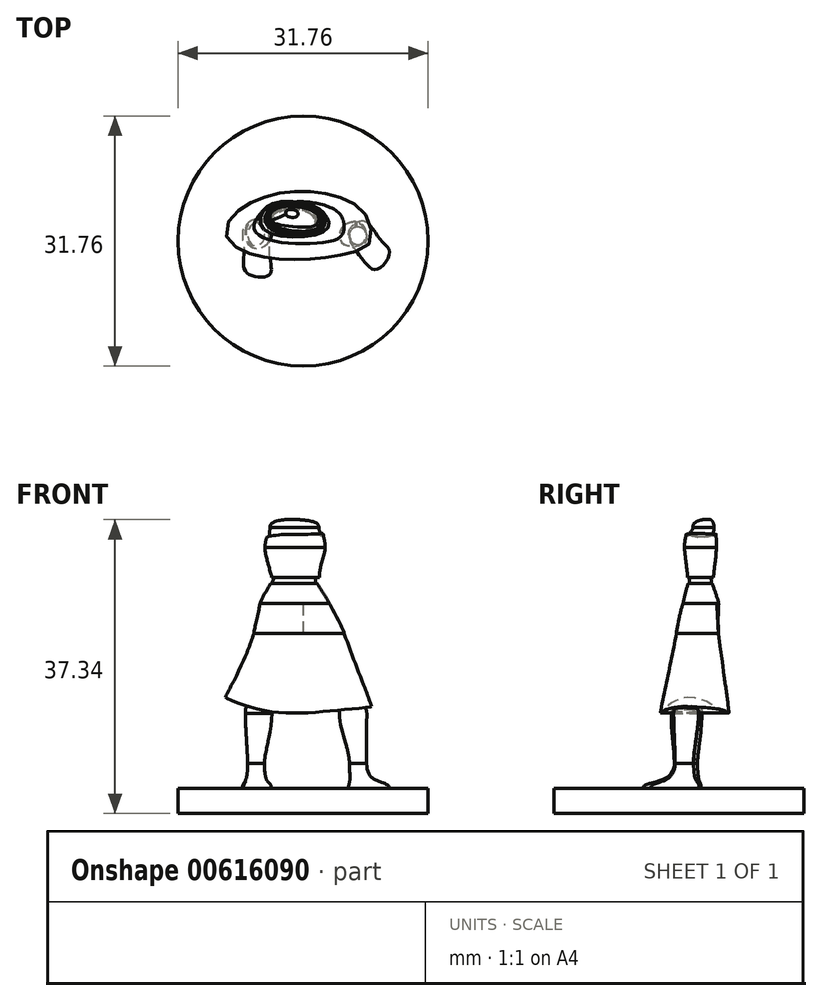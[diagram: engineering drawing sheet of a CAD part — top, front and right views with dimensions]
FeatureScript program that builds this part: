
annotation { "Feature Type Name" : "Feature", "Feature Type Description" : "" }
export const myFeature = defineFeature(function(context is Context, id is Id, definition is map)
    precondition{}
    {
        {
            var Q0;
            Q0=qCreatedBy(makeId("Top.planeOp"),FACE);
            var sketch = newSketch(context, id + "F0", { "sketchPlane" : qUnion([Q0])});
            skCircle(sketch, "E0", {"center": v(0, 0) * mm, "radius": 15.88 * mm});
            skSolve(sketch);
        }
        {
            var Q0;
            Q0 = qSketchRegion(id + "F0", true);
            extrude(context, id + "F1", {"entities" : qUnion([Q0]), "depth" : 3.17 * mm, "offsetDistance" : 25.4 * mm});
        }
        {
            var Q0;
            Q0=makeQuery(id+"F1.opExtrude","CAP_FACE",FACE,{"disambiguationData":[OSD([sQuery(id+"F0.wireOp",EDGE,"E0")])],"isStart":false});
            var sketch = newSketch(context, id + "F2", { "sketchPlane" : qUnion([Q0])});
            skFitSpline(sketch, "E1", {"points": [v(-5.78, 2.8) * mm, v(-7.59, 1.5) * mm, v(-7.5, -1.21) * mm, v(-7.18, -4) * mm, v(-4.3, -4.33) * mm, v(-4.23, -2.11) * mm, v(-4.47, 1.57) * mm, v(-5.78, 2.8) * mm]});
            skFitSpline(sketch, "E2.MirrorC", {"points": [v(6.74, 2.33) * mm, v(7.96, 2.46) * mm, v(9.84, 0.2) * mm, v(10.97, -1.52) * mm, v(9.33, -3.6) * mm, v(7.59, -2.35) * mm, v(5.78, 0.87) * mm, v(6.74, 2.33) * mm]});
            skSolve(sketch);
        }
        {
            var Q0;
            Q0=makeQuery(id+"F2.imprint","IMPRINT",FACE,{"disambiguationData":[TD([[makeQuery(id+"F2.imprint","IMPRINT",EDGE,{"derivedFrom":sQuery(id+"F2.wireOp",EDGE,"E1")}),-1.0]])]});
            cPlane(context, id + "F3", {"entities" : qUnion([Q0]), "cplaneType" : CPlaneType.OFFSET, "offset" : 3.17 * mm, "width" : 152.4 * mm, "height" : 152.4 * mm});
        }
        {
            var Q0;
            Q0=qCreatedBy(id+"F3.planeOp",FACE);
            var sketch = newSketch(context, id + "F4", { "sketchPlane" : qUnion([Q0])});
            skFitSpline(sketch, "E3", {"points": [v(-5.9, 2.34) * mm, v(-6.92, 1.45) * mm, v(-6.85, 0) * mm, v(-6.07, -0.6) * mm, v(-5.07, 0) * mm, v(-5.02, 1.24) * mm, v(-5.9, 2.34) * mm]});
            skFitSpline(sketch, "E4.MirrorC", {"points": [v(6.63, 1.8) * mm, v(7.62, 1.57) * mm, v(8.08, 0.56) * mm, v(7.62, -0.44) * mm, v(6.3, -0.24) * mm, v(5.9, 0.96) * mm, v(6.63, 1.8) * mm]});
            skSolve(sketch);
        }
        {
            var Q0;
            Q0=qCreatedBy(id+"F3.planeOp",FACE);
            cPlane(context, id + "F5", {"entities" : qUnion([Q0]), "cplaneType" : CPlaneType.OFFSET, "offset" : 6.35 * mm, "width" : 152.4 * mm, "height" : 152.4 * mm});
        }
        {
            var Q0;
            Q0=qCreatedBy(id+"F5.planeOp",FACE);
            cPlane(context, id + "F6", {"entities" : qUnion([Q0]), "cplaneType" : CPlaneType.OFFSET, "offset" : 1.9 * mm, "width" : 152.4 * mm, "height" : 152.4 * mm});
        }
        {
            var Q0;
            Q0=qCreatedBy(id+"F5.planeOp",FACE);
            cPlane(context, id + "F7", {"entities" : qUnion([Q0]), "cplaneType" : CPlaneType.OFFSET, "offset" : 10.16 * mm, "width" : 152.4 * mm, "height" : 152.4 * mm});
        }
        {
            var Q0;
            Q0=qCreatedBy(id+"F5.planeOp",FACE);
            var sketch = newSketch(context, id + "F8", { "sketchPlane" : qUnion([Q0])});
            skFitSpline(sketch, "E5", {"points": [v(8.1, 3.4) * mm, v(8.82, 0) * mm, v(6.73, -1.38) * mm, v(-2.75, -2.33) * mm, v(-10.34, 0) * mm, v(-10.24, 2.35) * mm, v(-3.65, 5.97) * mm, v(4.32, 5.69) * mm, v(8.1, 3.4) * mm]});
            skSolve(sketch);
        }
        {
            var Q0;
            Q0=qCreatedBy(id+"F7.planeOp",FACE);
            var sketch = newSketch(context, id + "F9", { "sketchPlane" : qUnion([Q0])});
            skFitSpline(sketch, "E6", {"points": [v(2.93, 4.47) * mm, v(4.91, 3.07) * mm, v(4.96, 0.8) * mm, v(2.58, -0.18) * mm, v(-3.74, 0) * mm, v(-6.25, 1.64) * mm, v(-5.25, 3.6) * mm, v(-2.9, 4.7) * mm, v(0, 4.98) * mm, v(2.93, 4.47) * mm]});
            skSolve(sketch);
        }
        {
            var Q1;
            Q1=makeQuery(id+"F8.imprint","IMPRINT",FACE,{"disambiguationData":[TD([[makeQuery(id+"F8.imprint","IMPRINT",EDGE,{"derivedFrom":sQuery(id+"F8.wireOp",EDGE,"E5")}),-1.0]])]});
            var Q2;
            Q2=makeQuery(id+"F9.imprint","IMPRINT",FACE,{"disambiguationData":[TD([[makeQuery(id+"F9.imprint","IMPRINT",EDGE,{"derivedFrom":sQuery(id+"F9.wireOp",EDGE,"E6")}),-1.0]])]});
            loft(context, id + "F10", {"operationType" : NewBodyOperationType.ADD, "startCondition" : LoftEndDerivativeType.NORMAL_TO_PROFILE, "startMagnitude" : .2, "sheetProfilesArray" : [{ "sheetProfileEntities" : qUnion([Q1]) }, { "sheetProfileEntities" : qUnion([Q2]) }]});
        }
        {
            var Q0;
            Q0=qCreatedBy(makeId("Front.planeOp"),FACE);
            var sketch = newSketch(context, id + "F11", { "sketchPlane" : qUnion([Q0])});
            skFitSpline(sketch, "E7", {"points": [v(-10.67, 15.18) * mm, v(-3.74, 12.9) * mm, v(4.93, 13.16) * mm, v(9.36, 13.75) * mm, v(10.68, 14.06) * mm, v(11.69, 13.41) * mm], "startDerivative": vector(18.49, -10.98) * mm, "endDerivative": vector(3.77, 1.33) * mm});
            skLineSegment(sketch, "E8", {"start": v(-10.67, 15.18) * mm, "end": v(-12.58, 9.38) * mm});
            skLineSegment(sketch, "E9", {"start": v(-12.58, 9.38) * mm, "end": v(13.84, 9.38) * mm});
            skLineSegment(sketch, "E10", {"start": v(13.84, 9.38) * mm, "end": v(11.69, 13.41) * mm});
            skLineSegment(sketch, "E11", {"start": v(-10.67, 15.18) * mm, "end": v(-10.44, 15.05) * mm});
            skLineSegment(sketch, "E12", {"start": v(11.69, 13.41) * mm, "end": v(11.69, 13.41) * mm});
            skSolve(sketch);
        }
        {
            var Q0;
            Q0 = qSketchRegion(id + "F11", true);
            extrude(context, id + "F12", {"entities" : qUnion([Q0]), "operationType" : NewBodyOperationType.REMOVE, "endBound" : BoundingType.SYMMETRIC, "oppositeDirection" : true, "depth" : 25.4 * mm, "offsetDistance" : 25.4 * mm});
        }
        {
            var Q1;
            Q1=makeQuery(id+"F2.imprint","IMPRINT",FACE,{"disambiguationData":[TD([[makeQuery(id+"F2.imprint","IMPRINT",EDGE,{"derivedFrom":sQuery(id+"F2.wireOp",EDGE,"E1")}),1.0]])]});
            var Q2;
            Q2=makeQuery(id+"F4.imprint","IMPRINT",FACE,{"disambiguationData":[TD([[makeQuery(id+"F4.imprint","IMPRINT",EDGE,{"derivedFrom":sQuery(id+"F4.wireOp",EDGE,"E3")}),1.0]])]});
            loft(context, id + "F13", {"operationType" : NewBodyOperationType.ADD, "startCondition" : LoftEndDerivativeType.NORMAL_TO_PROFILE, "startMagnitude" : 1, "endCondition" : LoftEndDerivativeType.NORMAL_TO_PROFILE, "endMagnitude" : 2.5, "sheetProfilesArray" : [{ "sheetProfileEntities" : qUnion([Q1]) }, { "sheetProfileEntities" : qUnion([Q2]) }]});
        }
        {
            var Q0;
            Q0=qCreatedBy(id+"F5.planeOp",FACE);
            var sketch = newSketch(context, id + "F14", { "sketchPlane" : qUnion([Q0])});
            skFitSpline(sketch, "E13", {"points": [v(-4.86, 2.7) * mm, v(-3.97, 1.02) * mm, v(-5.22, -0.86) * mm, v(-6.86, -0.54) * mm, v(-7.18, 1.88) * mm, v(-6.13, 2.8) * mm, v(-4.86, 2.7) * mm]});
            skSolve(sketch);
        }
        {
            var Q1;
            Q1=makeQuery(id+"F14.imprint","IMPRINT",FACE,{"disambiguationData":[TD([[makeQuery(id+"F14.imprint","IMPRINT",EDGE,{"derivedFrom":sQuery(id+"F14.wireOp",EDGE,"E13")}),-1.0]])]});
            var Q2;
            Q2=makeQuery(id+"F13.opLoft","CAP_FACE",FACE,{"disambiguationData":[OSD([makeQuery(id+"F4.imprint","IMPRINT",FACE,{"disambiguationData":[TD([[makeQuery(id+"F4.imprint","IMPRINT",EDGE,{"derivedFrom":sQuery(id+"F4.wireOp",EDGE,"E3")}),1.0]])]})])],"isStart":true});
            loft(context, id + "F15", {"operationType" : NewBodyOperationType.ADD, "startCondition" : LoftEndDerivativeType.NORMAL_TO_PROFILE, "startMagnitude" : 1.2, "endCondition" : LoftEndDerivativeType.NORMAL_TO_PROFILE, "endMagnitude" : .7, "sheetProfilesArray" : [{ "sheetProfileEntities" : qUnion([Q1]) }, { "sheetProfileEntities" : qUnion([Q2]) }]});
        }
        {
            var Q0;
            Q0=qCreatedBy(id+"F6.planeOp",FACE);
            var sketch = newSketch(context, id + "F16", { "sketchPlane" : qUnion([Q0])});
            skFitSpline(sketch, "E14", {"points": [v(-5.7, 2.62) * mm, v(-6.87, 1.8) * mm, v(-6.8, 0) * mm, v(-5.7, -0.65) * mm, v(-4.46, 0.67) * mm, v(-4.72, 2.14) * mm, v(-5.7, 2.62) * mm]});
            skSolve(sketch);
        }
        {
            var Q1;
            Q1=makeQuery(id+"F15.opLoft","CAP_FACE",FACE,{"disambiguationData":[OSD([makeQuery(id+"F14.imprint","IMPRINT",FACE,{"disambiguationData":[TD([[makeQuery(id+"F14.imprint","IMPRINT",EDGE,{"derivedFrom":sQuery(id+"F14.wireOp",EDGE,"E13")}),-1.0]])]})])],"isStart":true});
            var Q2;
            Q2=makeQuery(id+"F16.imprint","IMPRINT",FACE,{"disambiguationData":[TD([[makeQuery(id+"F16.imprint","IMPRINT",EDGE,{"derivedFrom":sQuery(id+"F16.wireOp",EDGE,"E14")}),1.0]])]});
            loft(context, id + "F17", {"operationType" : NewBodyOperationType.ADD, "startCondition" : LoftEndDerivativeType.NORMAL_TO_PROFILE, "startMagnitude" : 1, "sheetProfilesArray" : [{ "sheetProfileEntities" : qUnion([Q1]) }, { "sheetProfileEntities" : qUnion([Q2]) }]});
        }
        {
            var Q1;
            Q1=makeQuery(id+"F2.imprint","IMPRINT",FACE,{"disambiguationData":[TD([[makeQuery(id+"F2.imprint","IMPRINT",EDGE,{"derivedFrom":sQuery(id+"F2.wireOp",EDGE,"E2.MirrorC")}),-1.0]])]});
            var Q2;
            Q2=makeQuery(id+"F4.imprint","IMPRINT",FACE,{"disambiguationData":[TD([[makeQuery(id+"F4.imprint","IMPRINT",EDGE,{"derivedFrom":sQuery(id+"F4.wireOp",EDGE,"E4.MirrorC")}),-1.0]])]});
            loft(context, id + "F18", {"operationType" : NewBodyOperationType.ADD, "startCondition" : LoftEndDerivativeType.NORMAL_TO_PROFILE, "startMagnitude" : 1, "endCondition" : LoftEndDerivativeType.NORMAL_TO_PROFILE, "endMagnitude" : 2.5, "sheetProfilesArray" : [{ "sheetProfileEntities" : qUnion([Q1]) }, { "sheetProfileEntities" : qUnion([Q2]) }]});
        }
        {
            var Q0;
            Q0=qCreatedBy(id+"F5.planeOp",FACE);
            var sketch = newSketch(context, id + "F19", { "sketchPlane" : qUnion([Q0])});
            skFitSpline(sketch, "E15", {"points": [v(5.9, 2.34) * mm, v(4.76, 1.41) * mm, v(4.93, -0.24) * mm, v(7.26, -0.51) * mm, v(8.09, 0.75) * mm, v(7.31, 2.27) * mm, v(5.9, 2.34) * mm]});
            skSolve(sketch);
        }
        {
            var Q0;
            Q0=makeQuery(id+"F4.imprint","IMPRINT",FACE,{"disambiguationData":[TD([[makeQuery(id+"F4.imprint","IMPRINT",EDGE,{"derivedFrom":sQuery(id+"F4.wireOp",EDGE,"E4.MirrorC")}),-1.0]])]});
            var Q1;
            Q1=makeQuery(id+"F19.imprint","IMPRINT",FACE,{"disambiguationData":[TD([[makeQuery(id+"F19.imprint","IMPRINT",EDGE,{"derivedFrom":sQuery(id+"F19.wireOp",EDGE,"E15")}),1.0]])]});
            loft(context, id + "F20", {"operationType" : NewBodyOperationType.ADD, "startCondition" : LoftEndDerivativeType.NORMAL_TO_PROFILE, "startMagnitude" : .7, "endCondition" : LoftEndDerivativeType.NORMAL_TO_PROFILE, "endMagnitude" : 1, "sheetProfilesArray" : [{ "sheetProfileEntities" : qUnion([Q0]) }, { "sheetProfileEntities" : qUnion([Q1]) }]});
        }
        {
            var Q0;
            Q0=qCreatedBy(id+"F6.planeOp",FACE);
            var sketch = newSketch(context, id + "F21", { "sketchPlane" : qUnion([Q0])});
            skFitSpline(sketch, "E16", {"points": [v(5.62, 1.93) * mm, v(4.93, 0.7) * mm, v(5.66, -0.27) * mm, v(7.39, 0.25) * mm, v(7.08, 1.74) * mm, v(5.62, 1.93) * mm]});
            skSolve(sketch);
        }
        {
            var Q0;
            Q0 = qSketchRegion(id + "F21", true);
            var Q1;
            Q1=makeQuery(id+"F20.opLoft","CAP_FACE",FACE,{"disambiguationData":[OSD([makeQuery(id+"F19.imprint","IMPRINT",FACE,{"disambiguationData":[TD([[makeQuery(id+"F19.imprint","IMPRINT",EDGE,{"derivedFrom":sQuery(id+"F19.wireOp",EDGE,"E15")}),1.0]])]})])],"isStart":true});
            loft(context, id + "F22", {"operationType" : NewBodyOperationType.ADD, "startCondition" : LoftEndDerivativeType.NORMAL_TO_PROFILE, "startMagnitude" : .1, "endCondition" : LoftEndDerivativeType.NORMAL_TO_PROFILE, "endMagnitude" : 1, "sheetProfilesArray" : [{ "sheetProfileEntities" : qUnion([Q0]) }, { "sheetProfileEntities" : qUnion([Q1]) }]});
        }
        {
            var Q0;
            Q0=qCreatedBy(id+"F7.planeOp",FACE);
            cPlane(context, id + "F23", {"entities" : qUnion([Q0]), "cplaneType" : CPlaneType.OFFSET, "offset" : 3.8 * mm, "width" : 152.4 * mm, "height" : 152.4 * mm});
        }
        {
            var Q0;
            Q0=qCreatedBy(id+"F23.planeOp",FACE);
            var sketch = newSketch(context, id + "F24", { "sketchPlane" : qUnion([Q0])});
            skFitSpline(sketch, "E17", {"points": [v(0, 4.79) * mm, v(2.55, 3.64) * mm, v(2.97, 1.45) * mm, v(-5, 1.5) * mm, v(-4.41, 4.42) * mm, v(0, 4.79) * mm]});
            skSolve(sketch);
        }
        {
            var Q1;
            Q1=makeQuery(id+"F24.imprint","IMPRINT",FACE,{"disambiguationData":[TD([[makeQuery(id+"F24.imprint","IMPRINT",EDGE,{"derivedFrom":sQuery(id+"F24.wireOp",EDGE,"E17")}),-1.0]])]});
            var Q2;
            Q2=makeQuery(id+"F10.opLoft","CAP_FACE",FACE,{"disambiguationData":[OSD([makeQuery(id+"F9.imprint","IMPRINT",FACE,{"disambiguationData":[TD([[makeQuery(id+"F9.imprint","IMPRINT",EDGE,{"derivedFrom":sQuery(id+"F9.wireOp",EDGE,"E6")}),-1.0]])]})])],"isStart":true});
            loft(context, id + "F25", {"operationType" : NewBodyOperationType.ADD, "startCondition" : LoftEndDerivativeType.TANGENT_TO_PROFILE, "startMagnitude" : .3, "endCondition" : LoftEndDerivativeType.NORMAL_TO_PROFILE, "endMagnitude" : .3, "sheetProfilesArray" : [{ "sheetProfileEntities" : qUnion([Q1]) }, { "sheetProfileEntities" : qUnion([Q2]) }]});
        }
        {
            var Q0;
            Q0=qCreatedBy(id+"F23.planeOp",FACE);
            cPlane(context, id + "F26", {"entities" : qUnion([Q0]), "cplaneType" : CPlaneType.OFFSET, "offset" : 2.54 * mm, "width" : 152.4 * mm, "height" : 152.4 * mm});
        }
        {
            var Q0;
            Q0=qCreatedBy(id+"F26.planeOp",FACE);
            var sketch = newSketch(context, id + "F27", { "sketchPlane" : qUnion([Q0])});
            skFitSpline(sketch, "E18", {"points": [v(-0.88, 4.2) * mm, v(-3.99, 3.38) * mm, v(-3.23, 1.6) * mm, v(1.45, 1.73) * mm, v(1.56, 3.16) * mm, v(-0.88, 4.2) * mm]});
            skSolve(sketch);
        }
        {
            var Q1;
            Q1=makeQuery(id+"F25.opLoft","CAP_FACE",FACE,{"disambiguationData":[OSD([makeQuery(id+"F24.imprint","IMPRINT",FACE,{"disambiguationData":[TD([[makeQuery(id+"F24.imprint","IMPRINT",EDGE,{"derivedFrom":sQuery(id+"F24.wireOp",EDGE,"E17")}),-1.0]])]})])],"isStart":true});
            var Q2;
            Q2=makeQuery(id+"F27.imprint","IMPRINT",FACE,{"disambiguationData":[TD([[makeQuery(id+"F27.imprint","IMPRINT",EDGE,{"derivedFrom":sQuery(id+"F27.wireOp",EDGE,"E18")}),1.0]])]});
            loft(context, id + "F28", {"operationType" : NewBodyOperationType.ADD, "startCondition" : LoftEndDerivativeType.NORMAL_TO_PROFILE, "startMagnitude" : .3, "sheetProfilesArray" : [{ "sheetProfileEntities" : qUnion([Q1]) }, { "sheetProfileEntities" : qUnion([Q2]) }]});
        }
        {
            var Q0;
            Q0=qCreatedBy(id+"F26.planeOp",FACE);
            var sketch = newSketch(context, id + "F29", { "sketchPlane" : qUnion([Q0])});
            skFitSpline(sketch, "E19", {"points": [v(-2.76, 3.9) * mm, v(-3.94, 2.9) * mm, v(-2.5, 1.52) * mm, v(1.4, 1.97) * mm, v(0.83, 3.5) * mm, v(-2.76, 3.9) * mm]});
            skSolve(sketch);
        }
        {
            var Q0;
            Q0=qCreatedBy(id+"F26.planeOp",FACE);
            cPlane(context, id + "F30", {"entities" : qUnion([Q0]), "cplaneType" : CPlaneType.OFFSET, "offset" : 0.89 * mm, "width" : 152.4 * mm, "height" : 152.4 * mm});
        }
        {
            var Q0;
            Q0=qCreatedBy(id+"F30.planeOp",FACE);
            var sketch = newSketch(context, id + "F31", { "sketchPlane" : qUnion([Q0])});
            skFitSpline(sketch, "E20", {"points": [v(1.48, 2.79) * mm, v(1.2, 1.78) * mm, v(-2.86, 1.62) * mm, v(-3.66, 2.87) * mm, v(-2.39, 3.98) * mm, v(0.39, 3.78) * mm, v(1.48, 2.79) * mm]});
            skSolve(sketch);
        }
        {
            var Q1;
            Q1 = qSketchRegion(id + "F31", true);
            var Q2;
            Q2 = qSketchRegion(id + "F29", true);
            loft(context, id + "F32", {"operationType" : NewBodyOperationType.ADD, "startCondition" : LoftEndDerivativeType.TANGENT_TO_PROFILE, "startMagnitude" : 1, "endCondition" : LoftEndDerivativeType.TANGENT_TO_PROFILE, "endMagnitude" : 1, "sheetProfilesArray" : [{ "sheetProfileEntities" : qUnion([Q1]) }, { "sheetProfileEntities" : qUnion([Q2]) }]});
        }
        {
            var Q0;
            Q0=qCreatedBy(id+"F26.planeOp",FACE);
            cPlane(context, id + "F33", {"entities" : qUnion([Q0]), "cplaneType" : CPlaneType.OFFSET, "offset" : 0.76 * mm, "width" : 152.4 * mm, "height" : 152.4 * mm});
        }
        {
            var Q0;
            Q0=qCreatedBy(id+"F33.planeOp",FACE);
            var sketch = newSketch(context, id + "F34", { "sketchPlane" : qUnion([Q0])});
            skFitSpline(sketch, "E21", {"points": [v(-2.78, 4.1) * mm, v(-0.98, 4.35) * mm, v(1.49, 3.53) * mm, v(1.99, 2.13) * mm, v(0, 1.2) * mm, v(-2.7, 1.32) * mm, v(-3.98, 2.64) * mm, v(-2.78, 4.1) * mm]});
            skSolve(sketch);
        }
        {
            var Q0;
            Q0=qCreatedBy(id+"F33.planeOp",FACE);
            cPlane(context, id + "F35", {"entities" : qUnion([Q0]), "cplaneType" : CPlaneType.OFFSET, "offset" : 3.8 * mm, "width" : 152.4 * mm, "height" : 152.4 * mm});
        }
        {
            var Q0;
            Q0=qCreatedBy(id+"F35.planeOp",FACE);
            var sketch = newSketch(context, id + "F36", { "sketchPlane" : qUnion([Q0])});
            skFitSpline(sketch, "E22", {"points": [v(-3.99, 4.24) * mm, v(-4.65, 2.07) * mm, v(-1.91, 0.8) * mm, v(1.43, 0.94) * mm, v(2.7, 1.93) * mm, v(2.02, 3.8) * mm, v(-3.99, 4.24) * mm]});
            skSolve(sketch);
        }
        {
            var Q1;
            Q1 = qSketchRegion(id + "F36", true);
            var Q2;
            Q2 = qSketchRegion(id + "F34", true);
            loft(context, id + "F37", {"operationType" : NewBodyOperationType.ADD, "startCondition" : LoftEndDerivativeType.NORMAL_TO_PROFILE, "startMagnitude" : 1, "endCondition" : LoftEndDerivativeType.NORMAL_TO_PROFILE, "endMagnitude" : .3, "sheetProfilesArray" : [{ "sheetProfileEntities" : qUnion([Q1]) }, { "sheetProfileEntities" : qUnion([Q2]) }]});
        }
        {
            var Q0;
            Q0=qCreatedBy(id+"F35.planeOp",FACE);
            cPlane(context, id + "F38", {"entities" : qUnion([Q0]), "cplaneType" : CPlaneType.OFFSET, "offset" : 1.9 * mm, "width" : 152.4 * mm, "height" : 152.4 * mm});
        }
        {
            var Q0;
            Q0=qCreatedBy(id+"F38.planeOp",FACE);
            var sketch = newSketch(context, id + "F39", { "sketchPlane" : qUnion([Q0])});
            skFitSpline(sketch, "E23", {"points": [v(-2.58, 4.6) * mm, v(-3.86, 3.78) * mm, v(-4.33, 2.64) * mm, v(-3.83, 1.84) * mm, v(-1.7, 1.13) * mm, v(0.26, 0.98) * mm, v(1.56, 1.2) * mm, v(2.47, 2.08) * mm, v(1.86, 3.75) * mm, v(-0.34, 4.56) * mm, v(-2.58, 4.6) * mm]});
            skSolve(sketch);
        }
        {
            var Q0;
            Q0 = qSketchRegion(id + "F39", true);
            var Q1;
            Q1 = qSketchRegion(id + "F36", true);
            loft(context, id + "F40", {"operationType" : NewBodyOperationType.ADD, "startCondition" : LoftEndDerivativeType.NORMAL_TO_PROFILE, "startMagnitude" : .1, "endCondition" : LoftEndDerivativeType.NORMAL_TO_PROFILE, "endMagnitude" : 2, "sheetProfilesArray" : [{ "sheetProfileEntities" : qUnion([Q0]) }, { "sheetProfileEntities" : qUnion([Q1]) }]});
        }
        {
            var Q0;
            Q0=qCreatedBy(makeId("Front.planeOp"),FACE);
            var sketch = newSketch(context, id + "F41", { "sketchPlane" : qUnion([Q0])});
            skFitSpline(sketch, "E24", {"points": [v(4.17, 36.12) * mm, v(-1.2, 35.47) * mm, v(-4.56, 35.14) * mm, v(-7.27, 34.74) * mm, v(1.5, 38.34) * mm, v(3.58, 37.72) * mm, v(4.17, 36.12) * mm]});
            skSolve(sketch);
        }
        {
            var Q0;
            Q0 = qSketchRegion(id + "F41", true);
            extrude(context, id + "F42", {"entities" : qUnion([Q0]), "operationType" : NewBodyOperationType.REMOVE, "endBound" : BoundingType.SYMMETRIC, "oppositeDirection" : true, "depth" : 25.4 * mm, "offsetDistance" : 25.4 * mm});
        }
        {
            var Q0;
            Q0=qCreatedBy(id+"F35.planeOp",FACE);
            cPlane(context, id + "F43", {"entities" : qUnion([Q0]), "cplaneType" : CPlaneType.OFFSET, "offset" : 0.89 * mm, "width" : 152.4 * mm, "height" : 152.4 * mm});
        }
        {
            var Q0;
            Q0=qCreatedBy(id+"F43.planeOp",FACE);
            var sketch = newSketch(context, id + "F44", { "sketchPlane" : qUnion([Q0])});
            skFitSpline(sketch, "E25", {"points": [v(-3.03, 4.16) * mm, v(-3.89, 3.57) * mm, v(-4.3, 2.74) * mm, v(-3.87, 2) * mm, v(-1.5, 1.15) * mm, v(1.37, 1.23) * mm, v(2.28, 1.99) * mm, v(2.02, 3.28) * mm, v(0.8, 4.04) * mm, v(-1.32, 4.32) * mm, v(-3.03, 4.16) * mm]});
            skSolve(sketch);
        }
        {
            var Q0;
            Q0=qCreatedBy(id+"F43.planeOp",FACE);
            cPlane(context, id + "F45", {"entities" : qUnion([Q0]), "cplaneType" : CPlaneType.OFFSET, "offset" : 1.65 * mm, "width" : 152.4 * mm, "height" : 152.4 * mm});
        }
        {
            var Q0;
            Q0=qCreatedBy(id+"F45.planeOp",FACE);
            var sketch = newSketch(context, id + "F46", { "sketchPlane" : qUnion([Q0])});
            skFitSpline(sketch, "E26", {"points": [v(-4.1, 2.57) * mm, v(-2.24, 1.95) * mm, v(1.5, 1.99) * mm, v(2, 2.9) * mm, v(1.38, 3.74) * mm, v(-2.35, 4.4) * mm, v(-4.1, 3.5) * mm, v(-4.1, 2.57) * mm]});
            skSolve(sketch);
        }
        {
            var Q1;
            Q1 = qSketchRegion(id + "F46", true);
            var Q2;
            Q2 = qSketchRegion(id + "F44", true);
            loft(context, id + "F47", {"operationType" : NewBodyOperationType.ADD, "startCondition" : LoftEndDerivativeType.NORMAL_TO_PROFILE, "startMagnitude" : 1, "endCondition" : LoftEndDerivativeType.NORMAL_TO_PROFILE, "endMagnitude" : 2, "sheetProfilesArray" : [{ "sheetProfileEntities" : qUnion([Q1]) }, { "sheetProfileEntities" : qUnion([Q2]) }]});
        }
        {
            var Q0;
            Q0=qCreatedBy(id+"F45.planeOp",FACE);
            cPlane(context, id + "F48", {"entities" : qUnion([Q0]), "cplaneType" : CPlaneType.OFFSET, "offset" : 1.02 * mm, "width" : 152.4 * mm, "height" : 152.4 * mm});
        }
        {
            var Q0;
            Q0=qCreatedBy(id+"F48.planeOp",FACE);
            var sketch = newSketch(context, id + "F49", { "sketchPlane" : qUnion([Q0])});
            skFitSpline(sketch, "E27", {"points": [v(-1.6, 3.99) * mm, v(-2.12, 3.86) * mm, v(-2.13, 3.3) * mm, v(-1.09, 3.02) * mm, v(-0.65, 3.34) * mm, v(-0.79, 3.8) * mm, v(-1.6, 3.99) * mm]});
            skSolve(sketch);
        }
        {
            var Q1;
            Q1=makeQuery(id+"F47.opLoft","CAP_FACE",FACE,{"disambiguationData":[OSD([makeQuery(id+"F46.imprint","IMPRINT",FACE,{"disambiguationData":[TD([[makeQuery(id+"F46.imprint","IMPRINT",EDGE,{"derivedFrom":sQuery(id+"F46.wireOp",EDGE,"E26")}),1.0]])]})])],"isStart":true});
            var Q2;
            Q2 = qSketchRegion(id + "F49", true);
            loft(context, id + "F50", {"operationType" : NewBodyOperationType.ADD, "startCondition" : LoftEndDerivativeType.NORMAL_TO_PROFILE, "startMagnitude" : 2, "sheetProfilesArray" : [{ "sheetProfileEntities" : qUnion([Q1]) }, { "sheetProfileEntities" : qUnion([Q2]) }]});
        }
    });
